# Revit family: DWO2_63_UN_Surface-mounted_ETK
name_source: partatom
category: Lighting Fixtures
units: mm (PartAtom-declared; Revit-internal decimal feet)

## family parameters
Always vertical = Yes
Cut with Voids When Loaded = No
Light Source = No
OmniClass Number = 23.80.70.11.14.11
OmniClass Title = Downlights
Part Type = Normal
Room Calculation Point = Yes
Round Connector Dimension = Use Diameter
Shared = No
Work Plane-Based = No

## types (8) — shared parameters
Apparent Load = 19 VA
Assembly Code = 63.0
Bundle = -
IfcExportAs = IfcLightFixtureType
IfcExportType = USERDEFINED
Lamp = LED
Manufacturer = ETK licht B.V.
Model = DWO.2
URL = https://www.etk.nl
Voltage = 230 V

## per-type parameters (varying)
| type | Light Source | Wattage Comments |
| DWO.2100.xx - 12W / 1250lm / 3000K | DWO.2 - Lightsource : DWO.2100.xx - 12W / 1250lm / 3000K | 12W |
| DWO.2103.xx - 12W / 1250lm / 3000K | DWO.2 - Lightsource : DWO.2103.xx - 12W / 1250lm / 3000K | 12W |
| DWO.2200.xx - 12W / 1300lm / 4000K | DWO.2 - Lightsource : DWO.2200.xx - 12W / 1300lm / 4000K | 12W |
| DWO.2203.xx - 12W / 1300lm / 4000K | DWO.2 - Lightsource : DWO.2203.xx - 12W / 1300lm / 4000K | 12W |
| DWO.2300.xx - 19W / 2050lm / 3000K | DWO.2 - Lightsource : DWO.2300.xx - 19W / 2050lm / 3000K | 19W |
| DWO.2303.xx - 19W / 2050lm / 3000K | DWO.2 - Lightsource : DWO.2303.xx - 19W / 2050lm / 3000K | 19W |
| DWO.2400.xx - 19W / 2100lm / 4000K | DWO.2 - Lightsource : DWO.2400.xx - 19W / 2100lm / 4000K | 19W |
| DWO.2403.xx - 19W / 2100lm / 4000K | DWO.2 - Lightsource : DWO.2403.xx - 19W / 2100lm / 4000K | 19W |

## geometry (parser evidence)
native form markers: Sweep x6
no freeform markers — native parametric forms only
